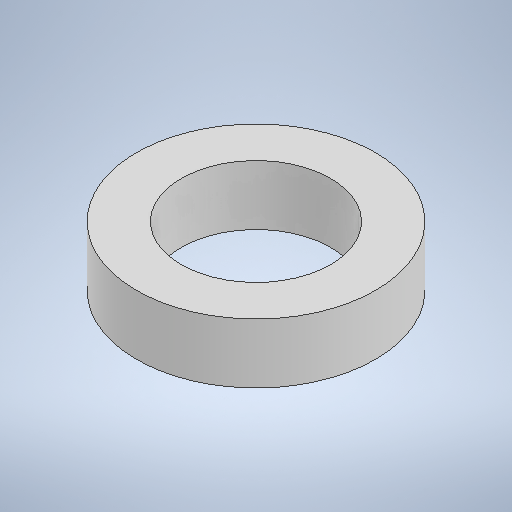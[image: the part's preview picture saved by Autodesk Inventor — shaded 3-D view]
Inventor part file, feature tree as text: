
AUTODESK INVENTOR PART (.ipt)
format: ipt  version: 2025.1 (Build 291241000, 241)  size: 259,072 bytes
history: native  units: mm
features: extrude x1, sketch x1
ambient origin geometry x8: Origin, YZ Plane, XZ Plane, XY Plane, X Axis, Y Axis, Z Axis, Center Point
bodies: Solid1 (feature_tree)
feature tree (2):
  extrude  "Extrusion1"  Depth=2.0mm
  sketch  "Sketch1"  dims[d0=8.0mm d1=5.0mm d2=2.0mm d3=0.0mm]
